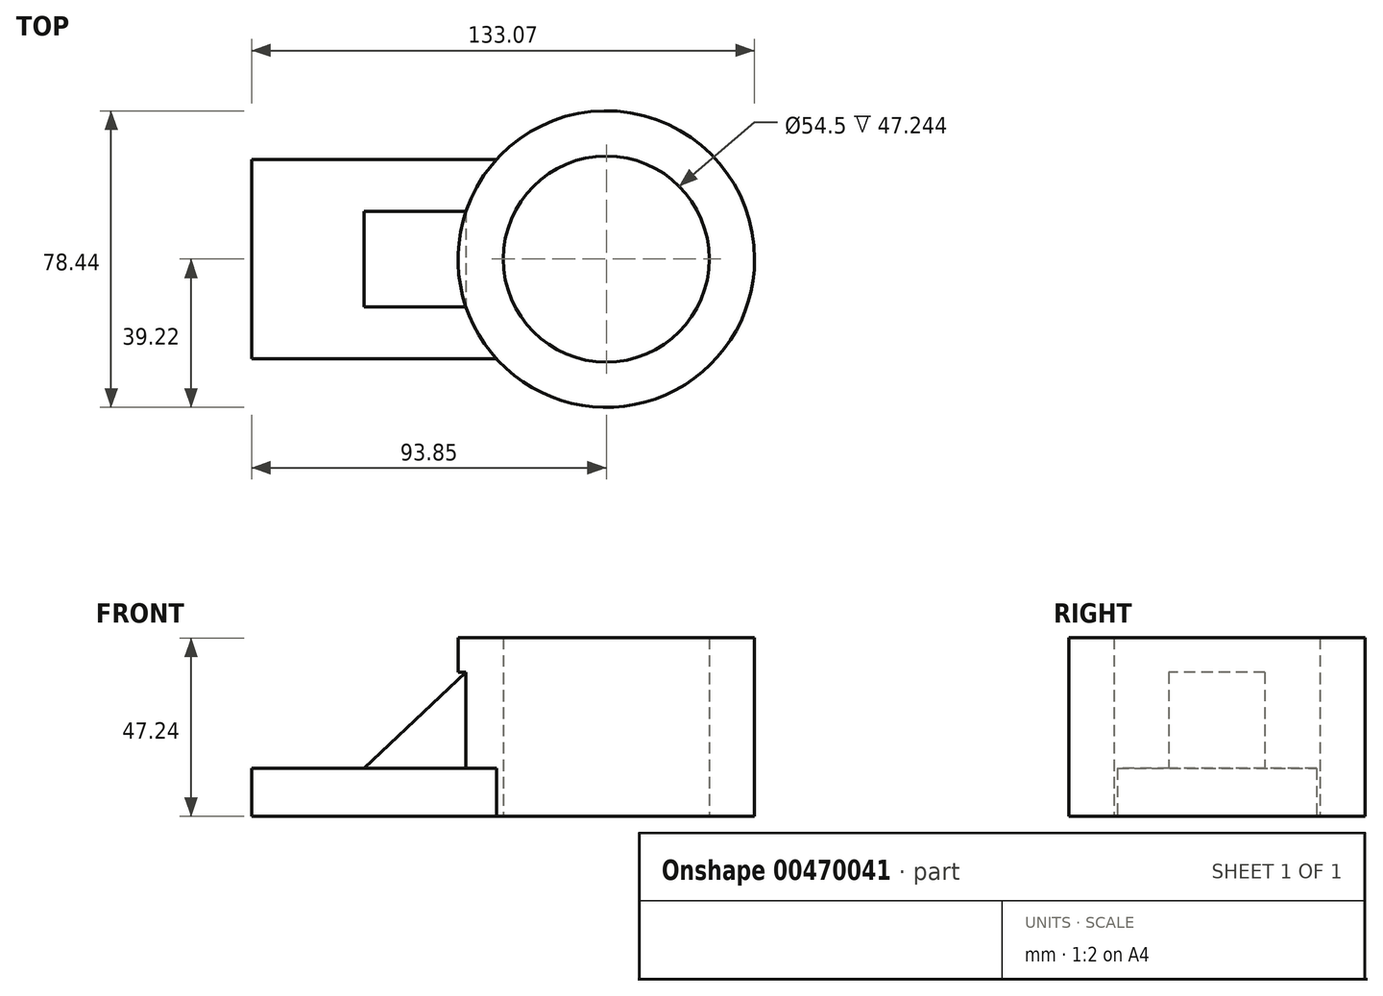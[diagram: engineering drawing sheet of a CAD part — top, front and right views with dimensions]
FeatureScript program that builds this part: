
annotation { "Feature Type Name" : "Feature", "Feature Type Description" : "" }
export const myFeature = defineFeature(function(context is Context, id is Id, definition is map)
    precondition{}
    {
        {
            var Q0;
            Q0=qCreatedBy(makeId("Top.planeOp"),FACE);
            var sketch = newSketch(context, id + "F0", { "sketchPlane" : qUnion([Q0])});
            skCircle(sketch, "E0", {"center": v(0, 0) * mm, "radius": 39.22 * mm});
            skCircle(sketch, "E1", {"center": v(0, 0) * mm, "radius": 27.25 * mm});
            skLineSegment(sketch, "E2", {"start": v(0, 0) * mm, "end": v(-115.46, 0) * mm, "construction": true});
            skLineSegment(sketch, "E3", {"start": v(-29.07, -26.33) * mm, "end": v(-93.85, -26.33) * mm});
            skLineSegment(sketch, "E4", {"start": v(-93.85, -26.33) * mm, "end": v(-93.85, 26.33) * mm});
            skLineSegment(sketch, "E5", {"start": v(-93.85, 26.33) * mm, "end": v(-29.07, 26.33) * mm});
            skSolve(sketch);
        }
        {
            var Q0;
            Q0=makeQuery(id+"F0.imprint","IMPRINT",FACE,{"disambiguationData":[TD([[makeQuery(id+"F0.imprint","IMPRINT",EDGE,{"derivedFrom":sQuery(id+"F0.wireOp",EDGE,"E1")}),-1.0]])]});
            extrude(context, id + "F1", {"entities" : qUnion([Q0]), "depth" : 47.24 * mm});
        }
        {
            var Q0;
            {var subQ0=sQuery(id+"F0.wireOp",EDGE,"E3");Q0=makeQuery(id+"F0.imprint","IMPRINT",FACE,{"disambiguationData":[TD([[makeQuery(id+"F0.imprint","IMPRINT",EDGE,{"derivedFrom":subQ0}),-1.0]])]});}
            extrude(context, id + "F2", {"entities" : qUnion([Q0]), "operationType" : NewBodyOperationType.ADD, "depth" : 12.7 * mm});
        }
        {
            var Q0;
            Q0=makeQuery(id+"F2.opExtrude","CAP_FACE",FACE,{"disambiguationData":[OSD([sQuery(id+"F0.wireOp",EDGE,"E0"),sQuery(id+"F0.wireOp",EDGE,"E3"),sQuery(id+"F0.wireOp",EDGE,"E4"),sQuery(id+"F0.wireOp",EDGE,"E5")])],"isStart":false});
            var sketch = newSketch(context, id + "F3", { "sketchPlane" : qUnion([Q0])});
            skLineSegment(sketch, "E6", {"start": v(-37.12, 12.68) * mm, "end": v(-64.12, 12.68) * mm});
            skLineSegment(sketch, "E7", {"start": v(-64.12, 12.68) * mm, "end": v(-64.12, -12.68) * mm});
            skLineSegment(sketch, "E8", {"start": v(-64.12, -12.68) * mm, "end": v(-37.12, -12.68) * mm});
            skSolve(sketch);
        }
        {
            var Q0;
            {var subQ0=sQuery(id+"F3.wireOp",EDGE,"E6");Q0=makeQuery(id+"F3.imprint","IMPRINT",FACE,{"disambiguationData":[TD([[makeQuery(id+"F3.imprint","IMPRINT",EDGE,{"derivedFrom":subQ0}),1.0]])]});}
            extrude(context, id + "F4", {"entities" : qUnion([Q0]), "operationType" : NewBodyOperationType.ADD, "depth" : 25.4 * mm});
        }
        {
            var Q0;
            Q0=makeQuery(id+"F4.opExtrude","SWEPT_FACE",FACE,{"disambiguationData":[OSD([sQuery(id+"F3.wireOp",EDGE,"E8")])]});
            var sketch = newSketch(context, id + "F5", { "sketchPlane" : qUnion([Q0])});
            skLineSegment(sketch, "E9", {"start": v(-37.12, 38.1) * mm, "end": v(-64.12, 12.7) * mm});
            skLineSegment(sketch, "E10", {"start": v(-64.12, 12.7) * mm, "end": v(-64.12, 38.1) * mm});
            skLineSegment(sketch, "E11", {"start": v(-64.12, 38.1) * mm, "end": v(-37.12, 38.1) * mm});
            skSolve(sketch);
        }
        {
            var Q0;
            Q0=makeQuery(id+"F5.imprint","IMPRINT",FACE,{"disambiguationData":[TD([[makeQuery(id+"F5.imprint","IMPRINT",EDGE,{"derivedFrom":sQuery(id+"F5.wireOp",EDGE,"E9")}),-1.0]])]});
            extrude(context, id + "F6", {"entities" : qUnion([Q0]), "operationType" : NewBodyOperationType.REMOVE, "endBound" : BoundingType.THROUGH_ALL, "oppositeDirection" : true, "depth" : 25.4 * mm});
        }
    });
